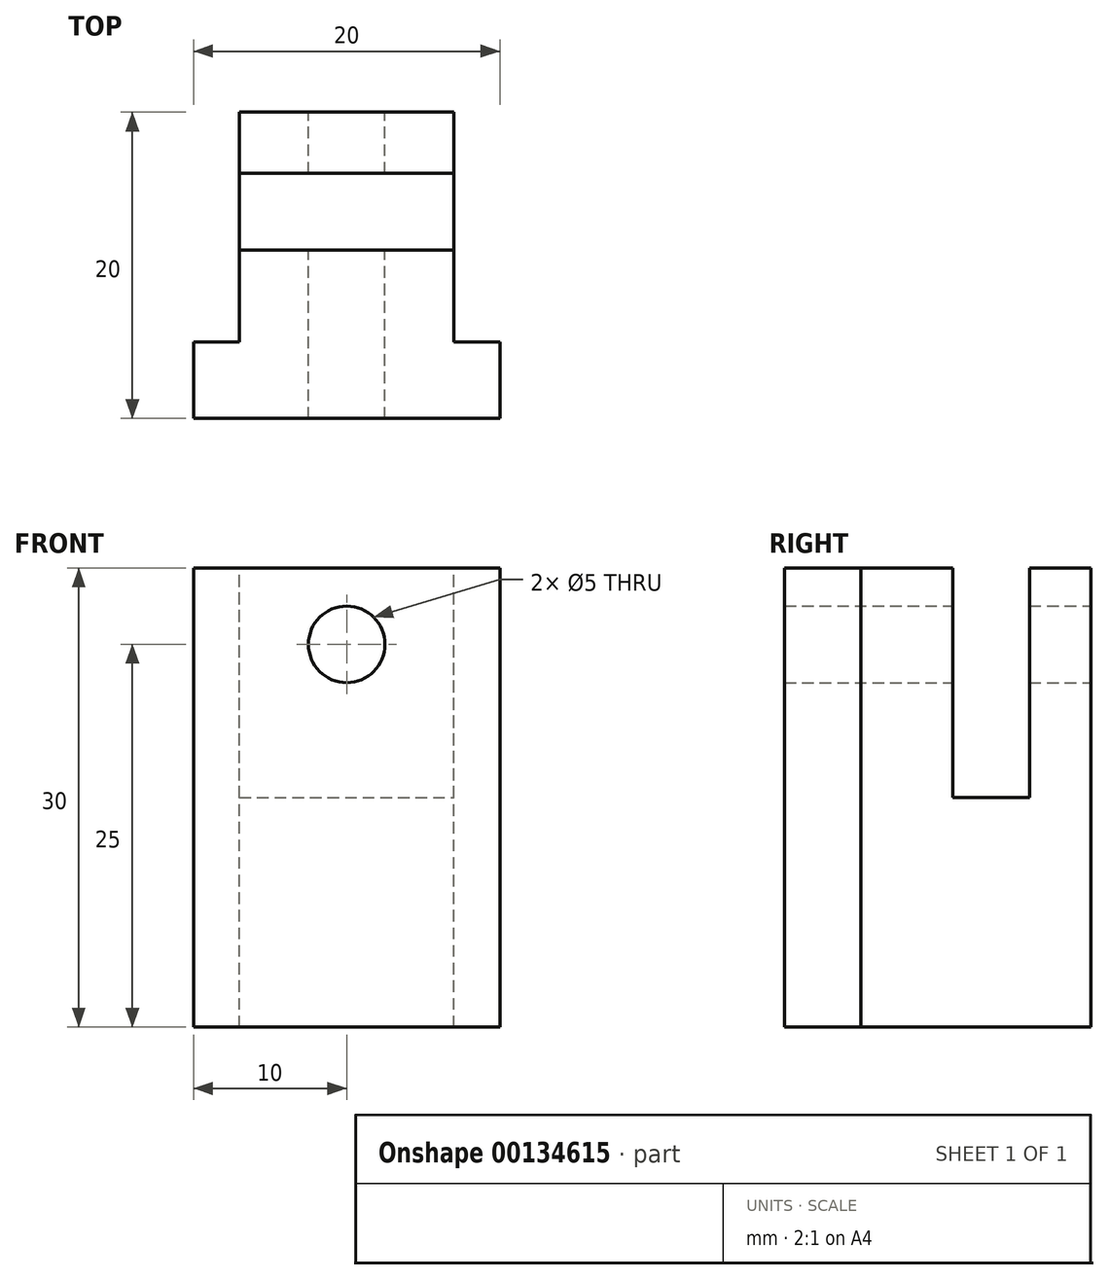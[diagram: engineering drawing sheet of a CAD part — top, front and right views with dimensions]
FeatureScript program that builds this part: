
annotation { "Feature Type Name" : "Feature", "Feature Type Description" : "" }
export const myFeature = defineFeature(function(context is Context, id is Id, definition is map)
    precondition{}
    {
        {
            var Q0;
            Q0=qCreatedBy(makeId("Top.planeOp"),FACE);
            var sketch = newSketch(context, id + "F0", { "sketchPlane" : qUnion([Q0])});
            skLineSegment(sketch, "E0", {"start": v(-10, 0) * mm, "end": v(10, 0) * mm});
            skLineSegment(sketch, "E1", {"start": v(10, 0) * mm, "end": v(10, 5) * mm});
            skLineSegment(sketch, "E2", {"start": v(10, 5) * mm, "end": v(7, 5) * mm});
            skLineSegment(sketch, "E3", {"start": v(7, 5) * mm, "end": v(7, 20) * mm});
            skLineSegment(sketch, "E4", {"start": v(7, 20) * mm, "end": v(-7, 20) * mm});
            skLineSegment(sketch, "E5", {"start": v(-7, 20) * mm, "end": v(-7, 5) * mm});
            skLineSegment(sketch, "E6", {"start": v(-7, 5) * mm, "end": v(-10, 5) * mm});
            skLineSegment(sketch, "E7", {"start": v(-10, 5) * mm, "end": v(-10, 0) * mm});
            skLineSegment(sketch, "E8.bottom", {"start": v(-7, 16) * mm, "end": v(7, 16) * mm});
            skLineSegment(sketch, "E8.top", {"start": v(-7, 11) * mm, "end": v(7, 11) * mm});
            skLineSegment(sketch, "E8.left", {"start": v(-7, 16) * mm, "end": v(-7, 11) * mm});
            skLineSegment(sketch, "E8.right", {"start": v(7, 16) * mm, "end": v(7, 11) * mm});
            skSolve(sketch);
        }
        {
            var Q0;
            {var subQ0=sQuery(id+"F0.wireOp",EDGE,"E4");Q0=makeQuery(id+"F0.imprint","IMPRINT",FACE,{"disambiguationData":[TD([[makeQuery(id+"F0.imprint","IMPRINT",EDGE,{"derivedFrom":subQ0}),1.0]])]});}
            var Q1;
            Q1=makeQuery(id+"F0.imprint","IMPRINT",FACE,{"disambiguationData":[TD([[makeQuery(id+"F0.imprint","IMPRINT",EDGE,{"derivedFrom":sQuery(id+"F0.wireOp",EDGE,"E8.bottom")}),-1.0]])]});
            var Q2;
            Q2=makeQuery(id+"F0.imprint","IMPRINT",FACE,{"disambiguationData":[TD([[makeQuery(id+"F0.imprint","IMPRINT",EDGE,{"derivedFrom":sQuery(id+"F0.wireOp",EDGE,"E0")}),1.0]])]});
            extrude(context, id + "F1", {"entities" : qUnion([Q0, Q1, Q2]), "oppositeDirection" : true, "depth" : 30 * mm});
        }
        {
            var Q0;
            Q0=makeQuery(id+"F1.opExtrude","CAP_FACE",FACE,{"disambiguationData":[OSD([sQuery(id+"F0.wireOp",EDGE,"E0"),sQuery(id+"F0.wireOp",EDGE,"E1"),sQuery(id+"F0.wireOp",EDGE,"E2"),sQuery(id+"F0.wireOp",EDGE,"E3"),sQuery(id+"F0.wireOp",EDGE,"E4"),sQuery(id+"F0.wireOp",EDGE,"E5"),sQuery(id+"F0.wireOp",EDGE,"E6"),sQuery(id+"F0.wireOp",EDGE,"E7"),sQuery(id+"F0.wireOp",EDGE,"E8.left"),sQuery(id+"F0.wireOp",EDGE,"E8.right")])],"isStart":true});
            var sketch = newSketch(context, id + "F2", { "sketchPlane" : qUnion([Q0])});
            skLineSegment(sketch, "E9.bottom", {"start": v(-7, 16) * mm, "end": v(7, 16) * mm});
            skLineSegment(sketch, "E9.top", {"start": v(-7, 11) * mm, "end": v(7, 11) * mm});
            skSolve(sketch);
        }
        {
            var Q0;
            {var subQ0=sQuery(id+"F2.wireOp",EDGE,"E9.bottom");Q0=makeQuery(id+"F2.imprint","IMPRINT",FACE,{"disambiguationData":[TD([[makeQuery(id+"F2.imprint","IMPRINT",EDGE,{"derivedFrom":subQ0}),-1.0]])]});}
            extrude(context, id + "F3", {"entities" : qUnion([Q0]), "operationType" : NewBodyOperationType.REMOVE, "oppositeDirection" : true, "depth" : 15 * mm});
        }
        {
            var Q0;
            Q0=makeQuery(id+"F1.opExtrude","SWEPT_FACE",FACE,{"disambiguationData":[OSD([sQuery(id+"F0.wireOp",EDGE,"E4")])]});
            var sketch = newSketch(context, id + "F4", { "sketchPlane" : qUnion([Q0])});
            skCircle(sketch, "E10", {"center": v(0, -5) * mm, "radius": 2.5 * mm});
            skPoint(sketch, "E10.centerSnap0", {"position": v(0, -30) * mm});
            skSolve(sketch);
        }
        {
            var Q0;
            Q0=makeQuery(id+"F4.imprint","IMPRINT",FACE,{"disambiguationData":[TD([[makeQuery(id+"F4.imprint","IMPRINT",EDGE,{"derivedFrom":sQuery(id+"F4.wireOp",EDGE,"E10")}),1.0]])]});
            extrude(context, id + "F5", {"entities" : qUnion([Q0]), "operationType" : NewBodyOperationType.REMOVE, "oppositeDirection" : true, "depth" : 25 * mm});
        }
    });
